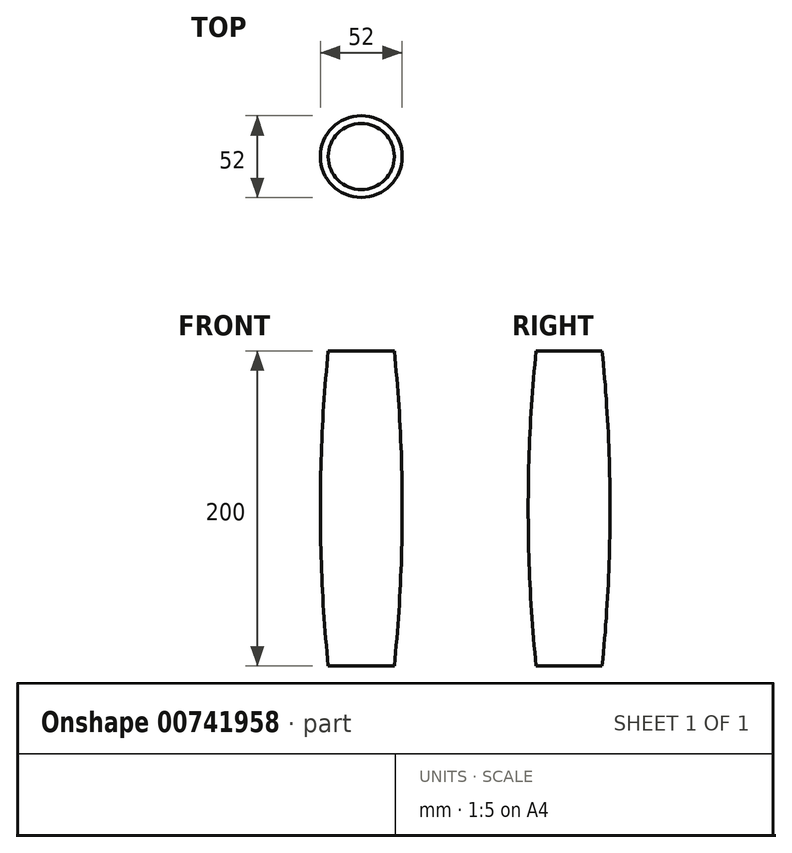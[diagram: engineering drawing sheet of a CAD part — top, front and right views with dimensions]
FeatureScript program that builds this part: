
annotation { "Feature Type Name" : "Feature", "Feature Type Description" : "" }
export const myFeature = defineFeature(function(context is Context, id is Id, definition is map)
    precondition{}
    {
        {
            var Q0;
            Q0=qCreatedBy(makeId("Front.planeOp"),FACE);
            var sketch = newSketch(context, id + "F0", { "sketchPlane" : qUnion([Q0])});
            skLineSegment(sketch, "E0", {"start": v(0, 0) * mm, "end": v(0, 100) * mm});
            skLineSegment(sketch, "E1", {"start": v(0, 100) * mm, "end": v(21, 100) * mm});
            skLineSegment(sketch, "E2", {"start": v(20.47, 105) * mm, "end": v(21, 100) * mm});
            skLineSegment(sketch, "E3", {"start": v(26, 0) * mm, "end": v(26, 0) * mm});
            skPoint(sketch, "E4.visualSharp", {"position": v(26, 52.64) * mm});
            skArc(sketch, "E4.filletArc", {"start": v(26, 0) * mm, "mid": v(24.62, 52.57) * mm, "end": v(20.47, 105) * mm});
            skArc(sketch, "E5.MirrorCS", {"start": v(26, 0) * mm, "mid": v(24.62, -52.57) * mm, "end": v(20.47, -105) * mm});
            skLineSegment(sketch, "E6.MirrorCS", {"start": v(20.47, -105) * mm, "end": v(21, -100) * mm});
            skLineSegment(sketch, "E7.MirrorCS", {"start": v(0, -100) * mm, "end": v(21, -100) * mm});
            skLineSegment(sketch, "E8.MirrorCS", {"start": v(0, 0) * mm, "end": v(0, -100) * mm});
            skSolve(sketch);
        }
        {
            var Q0;
            Q0=makeQuery(id+"F0.imprint","IMPRINT",FACE,{"disambiguationData":[TD([[makeQuery(id+"F0.imprint","IMPRINT",EDGE,{"derivedFrom":sQuery(id+"F0.wireOp",EDGE,"E0")}),-1.0]])]});
            var Q1;
            Q1=makeQuery(id+"F0.imprint","IMPRINT",FACE,{"disambiguationData":[TD([[makeQuery(id+"F0.imprint","IMPRINT",EDGE,{"derivedFrom":sQuery(id+"F0.wireOp",EDGE,"CjWrrxx0-ISEx-yxa1-8jfl-dFYM9Hkqyzem")}),1.0]])]});
            var Q2;
            Q2=sQuery(id+"F0.wireOp",EDGE,"E0");
            revolve(context, id + "F1", {"surfaceOperationType" : NewSurfaceOperationType.NEW, "entities" : qUnion([Q0, Q1]), "axis" : qUnion([Q2]), "revolveType" : RevolveType.FULL, "oppositeDirection" : true});
        }
    });
